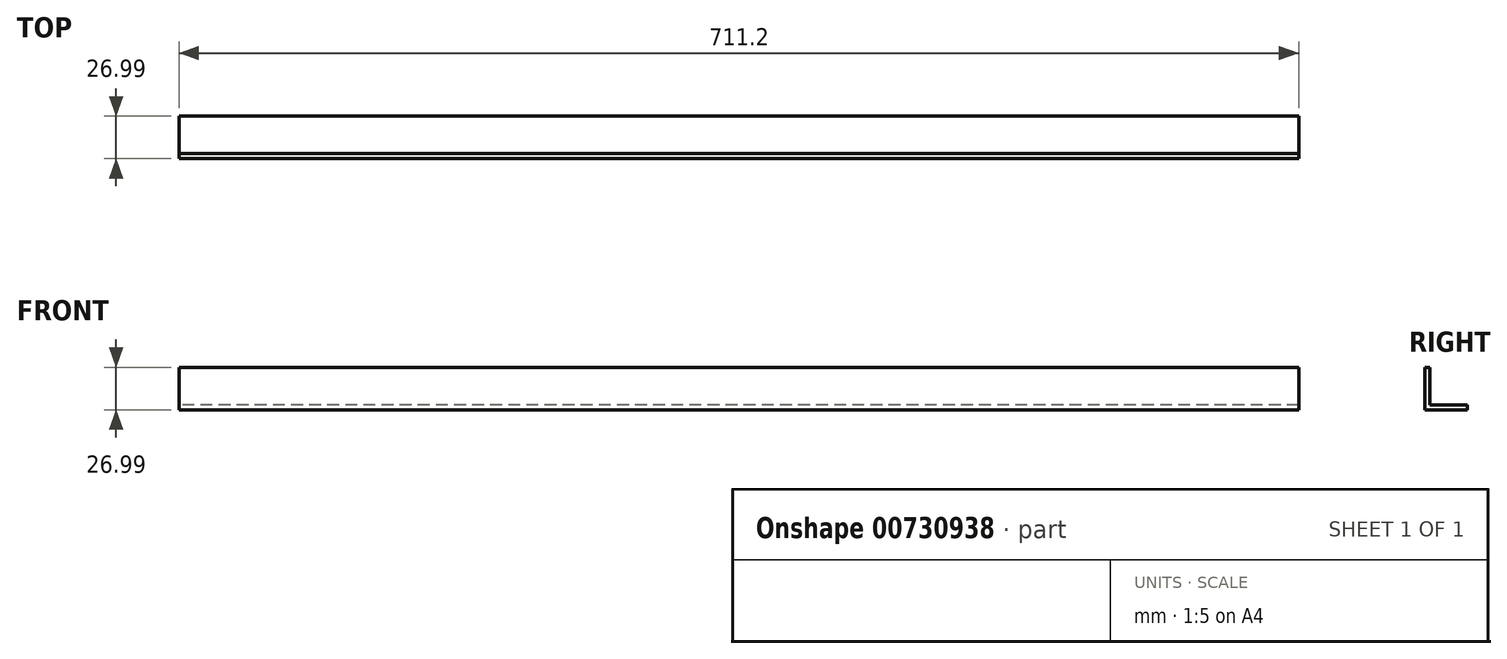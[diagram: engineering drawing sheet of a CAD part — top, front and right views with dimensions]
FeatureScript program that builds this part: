
annotation { "Feature Type Name" : "Feature", "Feature Type Description" : "" }
export const myFeature = defineFeature(function(context is Context, id is Id, definition is map)
    precondition{}
    {
        {
            var Q0;
            Q0=qCreatedBy(makeId("Right.planeOp"),FACE);
            var sketch = newSketch(context, id + "F0", { "sketchPlane" : qUnion([Q0])});
            skLineSegment(sketch, "E0", {"start": v(0, 0) * mm, "end": v(25.4, 0) * mm, "construction": true});
            skLineSegment(sketch, "E1", {"start": v(0, 0) * mm, "end": v(0, 25.4) * mm, "construction": true});
            skLineSegment(sketch, "E2.0", {"start": v(-1.59, -1.59) * mm, "end": v(-1.59, 25.4) * mm});
            skLineSegment(sketch, "E2.1", {"start": v(-1.59, -1.59) * mm, "end": v(25.4, -1.59) * mm});
            skLineSegment(sketch, "E3.0", {"start": v(1.59, 1.59) * mm, "end": v(1.59, 25.4) * mm});
            skLineSegment(sketch, "E3.1", {"start": v(1.59, 1.59) * mm, "end": v(25.4, 1.59) * mm});
            skLineSegment(sketch, "E4", {"start": v(-1.59, 25.4) * mm, "end": v(1.59, 25.4) * mm});
            skLineSegment(sketch, "E5", {"start": v(25.4, -1.59) * mm, "end": v(25.4, 1.59) * mm});
            skSolve(sketch);
        }
        {
            var Q0;
            Q0=makeQuery(id+"F0.imprint","IMPRINT",FACE,{"disambiguationData":[TD([[makeQuery(id+"F0.imprint","IMPRINT",EDGE,{"derivedFrom":sQuery(id+"F0.wireOp",EDGE,"E2.0")}),-1.0]])]});
            extrude(context, id + "F1", {"entities" : qUnion([Q0]), "depth" : 711.2 * mm, "offsetDistance" : 25.4 * mm});
        }
    });
